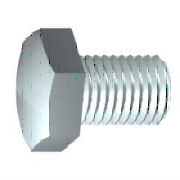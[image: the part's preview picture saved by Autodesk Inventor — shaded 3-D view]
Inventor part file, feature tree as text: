
AUTODESK INVENTOR PART (.ipt)
format: ipt  version: 2023 (Build 270158000, 158)  size: 220,160 bytes
history: native  units: mm
features: sketch x4, other x2, plane x1
ambient origin geometry x8: Origin, YZ Plane, XZ Plane, XY Plane, X Axis, Y Axis, Z Axis, Center Point
bodies: Solid1 (feature_tree)
feature tree (7):
  plane  "Work Plane1"
  sketch  "Sketch1"  dims[d6=0.6mm]
  sketch  "Sketch2"  dims[d7=11.63mm]
  sketch  "Sketch4"  dims[d9=135.0deg d10=8.0mm d11=16.0mm d13=90.0deg d14=13.0mm d15=0.0mm d16=0.6mm d17=2.0mm d18=45.0deg d19=13.0mm d20=15.011107mm d21=4.7mm d22=0.0mm d32=9.2mm d34=0.0mm d35=8.0mm d37=0.0mm d38=0.0mm d39=120.0deg d40=13.0mm d41=10.0mm d42=60.0deg d49=0.6mm d50=0.0mm]
  other  "Srf2"
  sketch  "Sketch3"  dims[d8=0.1mm]
  other  "Srf1"
